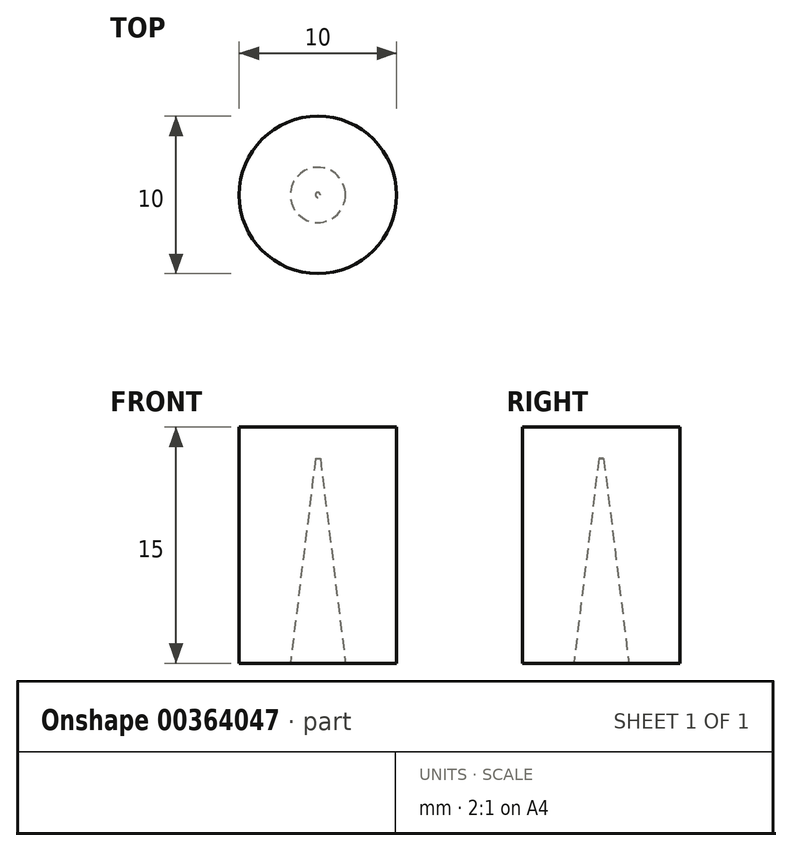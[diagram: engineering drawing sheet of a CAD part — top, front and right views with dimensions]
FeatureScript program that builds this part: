
annotation { "Feature Type Name" : "Feature", "Feature Type Description" : "" }
export const myFeature = defineFeature(function(context is Context, id is Id, definition is map)
    precondition{}
    {
        {
            var Q0;
            Q0=qCreatedBy(makeId("Top.planeOp"),FACE);
            var sketch = newSketch(context, id + "F0", { "sketchPlane" : qUnion([Q0])});
            skCircle(sketch, "E0", {"center": v(0, 0) * mm, "radius": 5 * mm});
            skSolve(sketch);
        }
        {
            var Q0;
            Q0 = qSketchRegion(id + "F0", true);
            extrude(context, id + "F1", {"entities" : qUnion([Q0]), "depth" : 15 * mm});
        }
        {
            var Q0;
            Q0=makeQuery(id+"F1.opExtrude","CAP_FACE",FACE,{"disambiguationData":[OSD([sQuery(id+"F0.wireOp",EDGE,"E0")])],"isStart":true});
            var sketch = newSketch(context, id + "F2", { "sketchPlane" : qUnion([Q0])});
            skCircle(sketch, "E1", {"center": v(0, 0) * mm, "radius": 1.75 * mm});
            skSolve(sketch);
        }
        {
            var Q0;
            Q0 = qSketchRegion(id + "F2", true);
            extrude(context, id + "F3", {"entities" : qUnion([Q0]), "operationType" : NewBodyOperationType.REMOVE, "oppositeDirection" : true, "depth" : 13 * mm, "hasDraft" : true, "draftAngle" : 7 * degree, "draftPullDirection" : true});
        }
    });
